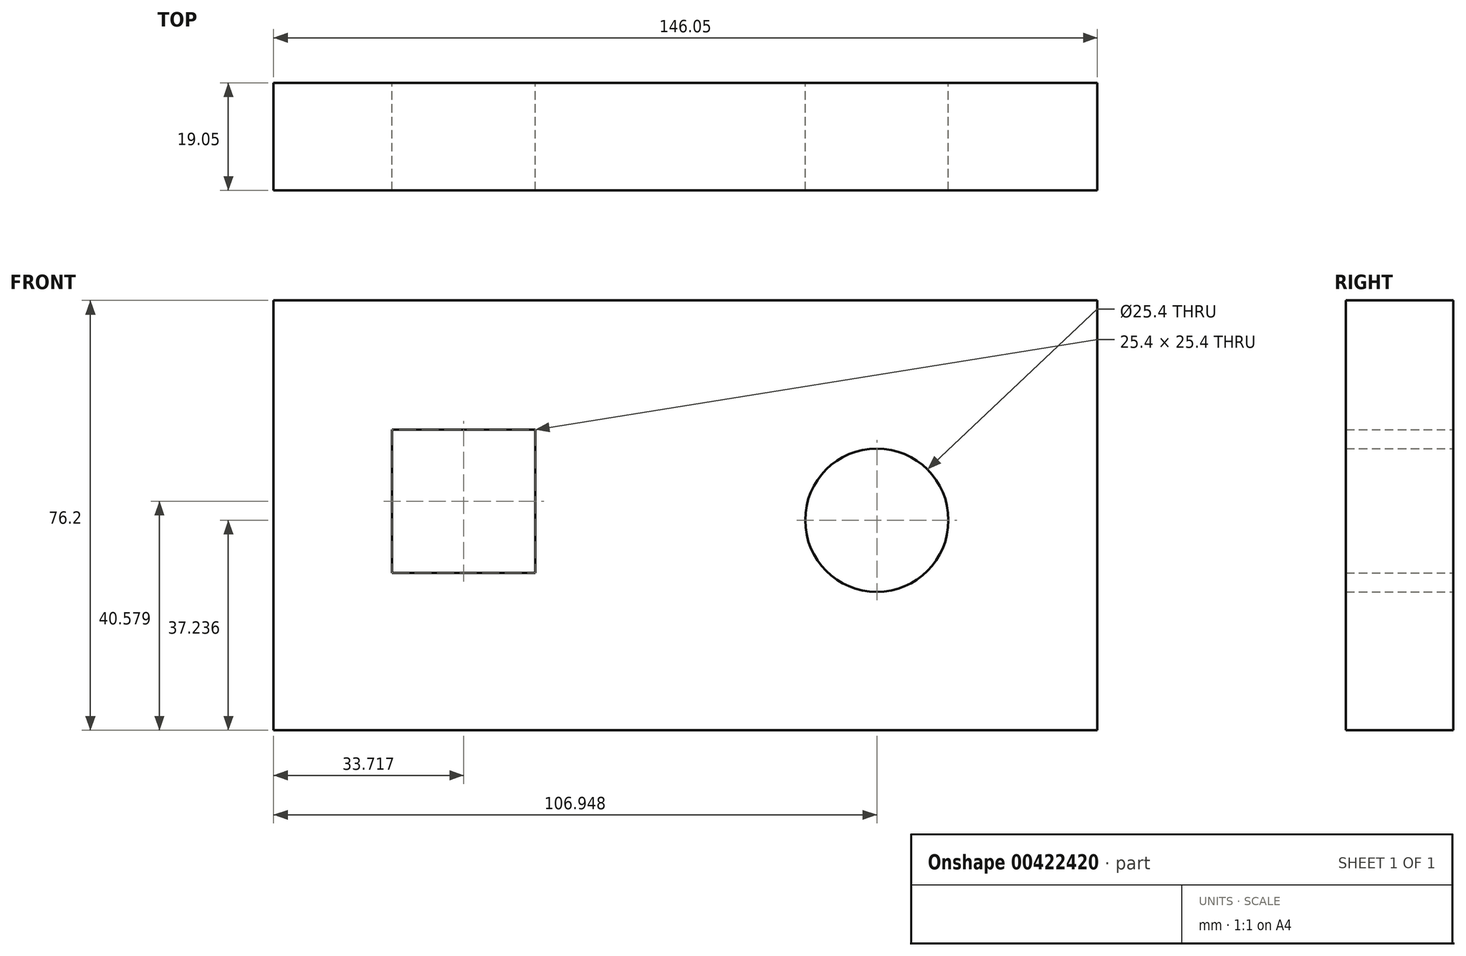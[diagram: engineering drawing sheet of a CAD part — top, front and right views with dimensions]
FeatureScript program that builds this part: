
annotation { "Feature Type Name" : "Feature", "Feature Type Description" : "" }
export const myFeature = defineFeature(function(context is Context, id is Id, definition is map)
    precondition{}
    {
        {
            var Q0;
            Q0=qCreatedBy(makeId("Front.planeOp"),FACE);
            var sketch = newSketch(context, id + "F0", { "sketchPlane" : qUnion([Q0])});
            skLineSegment(sketch, "E0", {"start": v(-71.24, 0) * mm, "end": v(74.8, 0) * mm});
            skLineSegment(sketch, "E1", {"start": v(74.8, 0) * mm, "end": v(74.8, 76.2) * mm});
            skLineSegment(sketch, "E2", {"start": v(74.8, 76.2) * mm, "end": v(-71.24, 76.2) * mm});
            skLineSegment(sketch, "E3", {"start": v(-71.24, 76.2) * mm, "end": v(-71.24, 0) * mm});
            skLineSegment(sketch, "E4.bottom", {"start": v(-50.22, 53.28) * mm, "end": v(-24.82, 53.28) * mm});
            skLineSegment(sketch, "E4.top", {"start": v(-50.22, 27.88) * mm, "end": v(-24.82, 27.88) * mm});
            skLineSegment(sketch, "E4.left", {"start": v(-50.22, 53.28) * mm, "end": v(-50.22, 27.88) * mm});
            skLineSegment(sketch, "E4.right", {"start": v(-24.82, 53.28) * mm, "end": v(-24.82, 27.88) * mm});
            skCircle(sketch, "E5", {"center": v(35.7, 37.24) * mm, "radius": 12.7 * mm});
            skSolve(sketch);
        }
        {
            var Q0;
            Q0 = qSketchRegion(id + "F0", true);
            extrude(context, id + "F1", {"entities" : qUnion([Q0]), "depth" : 19.05 * mm});
        }
        {
            var Q0;
            Q0 = qSketchRegion(id + "F0", true);
            extrude(context, id + "F2", {"entities" : qUnion([Q0]), "operationType" : NewBodyOperationType.ADD, "depth" : 19.05 * mm});
        }
    });
